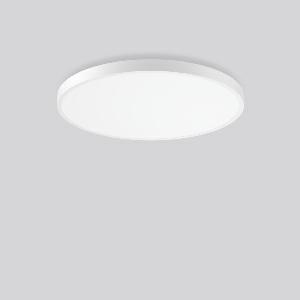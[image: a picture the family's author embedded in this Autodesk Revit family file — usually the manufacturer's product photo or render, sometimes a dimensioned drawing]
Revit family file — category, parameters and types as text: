
# Revit family: triona_round_a_312388_002_1_76_c8d4
name_source: partatom
category: Lighting Fixtures
units: mm (PartAtom-declared; Revit-internal decimal feet)

## family parameters
Cut with Voids When Loaded = No
Host = Face
Light Source = No
Part Type = Normal
Room Calculation Point = No
Round Connector Dimension = Use Diameter
Shared = No

## types (1)
- TRIONA round A (1 x LED Modul 840, 12900 lm, 4000)
    Apparent Load = 133 VA
    CIE Flux Codes = 49 80 96 71 100
    Color Rendering = 80
    Color Temperature = 4000
    Default Elevation = 1800 mm
    Description = Series: TRIONA round
Decorative round LED surface-mounted luminaire. Flat, seamless frame: aluminium extrusion profile, powder coated. Cover made of sheet steel, powder-coated. Direct light emission through a diffuser plastic opal. Indirect light emission through a flush diffuser made of satin-finish plastic. Lightguide and diffuser made of non-yellowing plastic (PMMA). Lateral light emission (RZB SIDELITE technology) for above-average homogeneous light distribution. Direct 70%, indirect 30% light emission. Suitable for Ceiling mounting, Wall (surface). Tool-free mounting via bayonet connection. Electronic ballast included. Very easy installation thanks to Plug+Play connection. 
Colour: traffic white, matt (RAL 9016)
Diameter: 845 mm
Height: 88 mm
Lamp: LED
Socket: without socket
Colour temperature: 4000K
Colour rendering index (CRI): 80
System power: 133 W
Rated luminous flux: 12900 lm
Luminous efficiency: 97 lm/W
Control gear: Converter, dimmable, DALI
Protection class: I
Type of protection: IP 20
    Height = 88 mm
    Lamp = 1 x LED Modul 840
    Lamp Light Flux = 12900 lm
    Lamp count = 1
    Length = 845 mm
    Lifetime = 50000 h
    Luminous efficacy = 97 lm/W
    Manufacturer = RZB
    ModVariant = No
    Model = 312388.002.1.76
    Mounting Place = Ceiling
    Mounting Type = Surface mounted
    Number of Poles = 1
    OnlyDefault = Yes
    Power Factor = 1
    Product Name = TRIONA round A
    Product group = Surface mounted modular luminaires
    ProductGroupID = 306
    Protection Class = Protection class I
    Protection Degree = IP 20
    RLX_Detail_Level = 1
    RLX_Emergency_Light_Flux = 0 lm
    RLX_Emergency_Type = 0
    RLX_Emergency_Type_DB = No
    RlxData = <blob elided: 40709 chars, md5=d3b6f992>
    Socket = socket
    Standby Power = 0 W
    System Light Flux = 12900 lm
    System Power = 133 W
    Type Comments = Product without accessories
    Type Image = 312388.002.jpg
    URL = http://relux.com
    VarID = ---
    Voltage = 230 V
    Voltage Range = 220-240 V
    Weight = 0.00 kg
    Width = 0 mm  [stored 0 ft]

note: [stored X ft] marks values corroborated as IEEE doubles in the binary element streams (Revit-internal decimal feet)

## geometry (parser evidence)
native form markers: Blend x4, Sweep x13
no freeform markers — native parametric forms only
